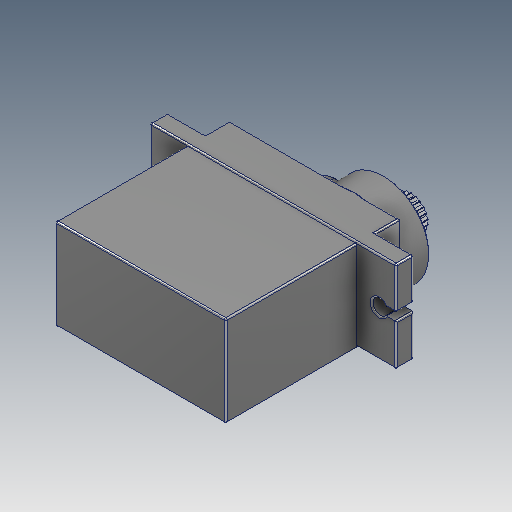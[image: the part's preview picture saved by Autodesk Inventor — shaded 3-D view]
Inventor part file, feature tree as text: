
AUTODESK INVENTOR PART (.ipt)
format: ipt  version: 2020 (Build 240168000, 168)  size: 304,640 bytes
history: mixed  units: mm
features: fillet x2, imported_body x1
ambient origin geometry x8: Origin, YZ Plane, XZ Plane, XY Plane, X Axis, Y Axis, Z Axis, Center Point
bodies: Solid1 (imported_parasolid), Solid2 (imported_parasolid)
feature tree (3):
  fillet  "Fillet1"  [1 undecoded]
  fillet  "Fillet3"  [1 undecoded]
  imported_body  NMx_Import_Brep_tag  [imported B-rep: ~32 faces, bbox_mm=[22.5, 11.8, 27.3]]
note: 2 required parameter values undecoded (feature->parameter linkage not recoverable at this tier; creation-order binding heuristic only, values carry confidence <= 0.55)
